# Revit family: LF8ML
name_source: partatom
category: Lighting Fixtures
revit_build: Autodesk Revit 2014 (Build: 20130308_1515(x64)
units: mm (PartAtom-declared; Revit-internal decimal feet)

## types (1)
- LF8SL
    Apparent Load = 39 VA
    Application = Education
Healthcare
Hospitality
Office
Lobby
Conference Room
Waiting Room
Classroom
Auditorium
Guest Room
Dining Area
    Color Filter = 16777215
    Default Elevation = 48.000"
    Description = Designed for optimal life and lumen maintenance, the LF8 is a 8 architectural LED downlight with color consistency from fixture to fixture.
    Dimming Lamp Color Temperature Shift = <None>
    Emit Shape Visible in Rendering = No
    Emit from Circle Diameter = 24.000"
    Features = Light Engine utilizes Philips Fortimo LED module and provides controlled color consistency
Universal 120-277V high efficiency LED driver with 0-10V dimming standard
1100, 1500, 2000, and 3000 lumen modules
Photometrics tested per IESNA-LM-79-2008 standards
Minimum 50,000 hours at 70% lumen maintenance
5-year warranty
Clear or Diffuse regressed lens option available with multiple colors and trim options.
SpectraSync™ Color Tuning Technology available
NX Distributed Intelligence™ wired and wireless controls capability available
    Glass = Glass
    Height = 7.750"
    Lamp = 1
    Length = 14.000"
    Load Classification = Lighting
    Manufacturer = Hubbell Healthcare Solutions
    Model = LF8ML
    Number of Poles = 1
    Photometric Web File = generic
    Power Factor = 0.9
    Product Documentation Link = https://hubbellcdn.com
    Product Material = Steel
    Product Page URL = https://www.hubbell.com
    Tilt Angle = 60.00°
    URL = https://www.hubbell.com
    Voltage = 120 V
    Wattage Comments = 14W
    Width = 12.625"

## geometry (parser evidence)
native form markers: Blend x1, Sweep x2
no freeform markers — native parametric forms only
